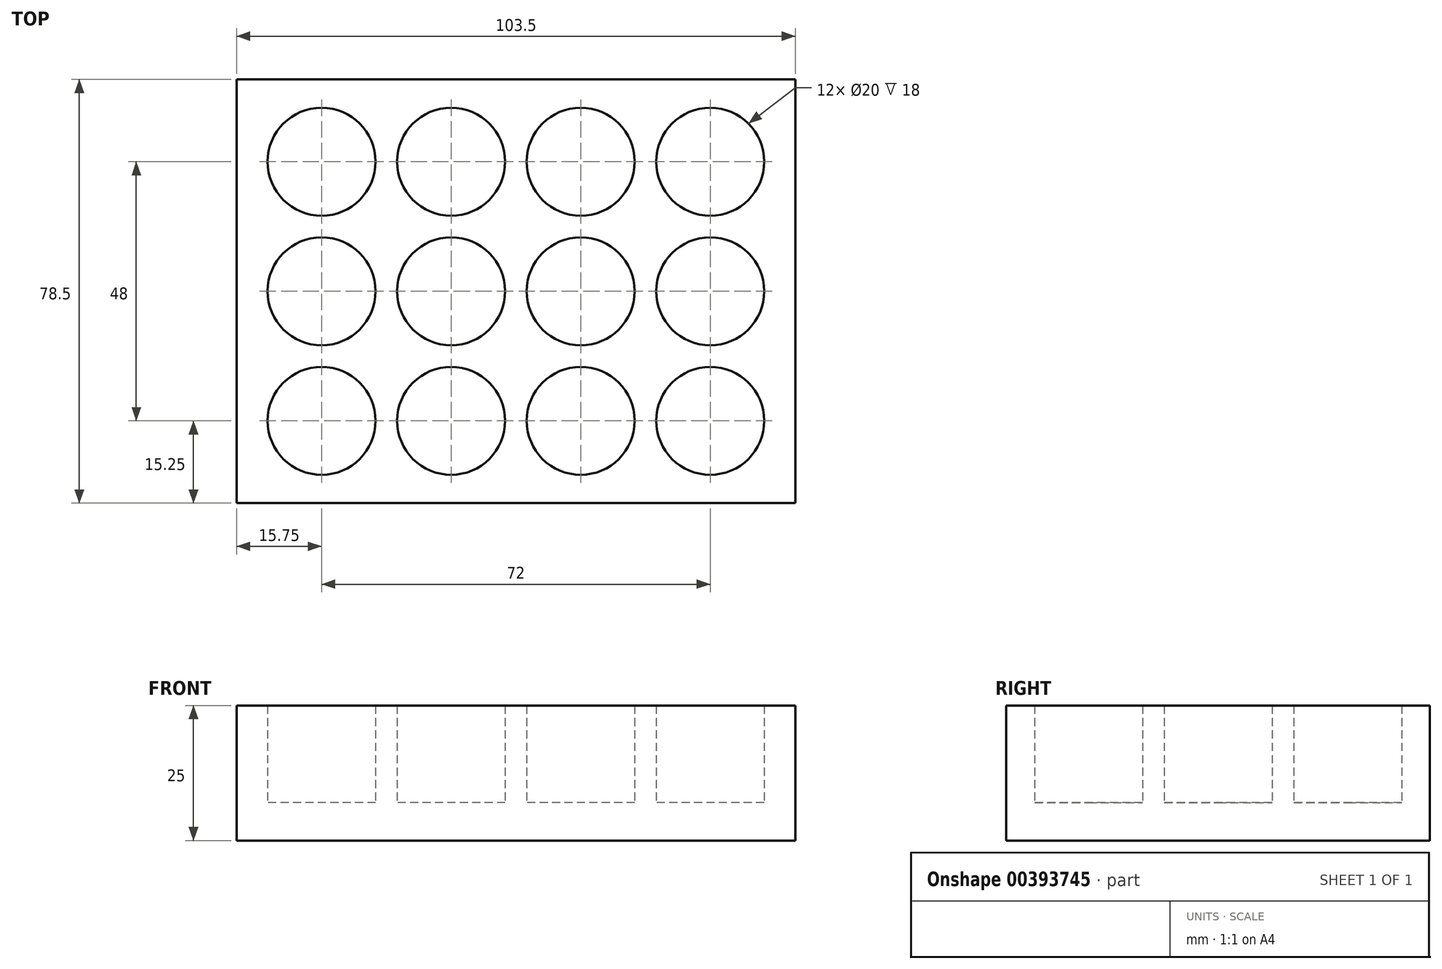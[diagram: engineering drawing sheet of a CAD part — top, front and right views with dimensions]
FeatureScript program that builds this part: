
annotation { "Feature Type Name" : "Feature", "Feature Type Description" : "" }
export const myFeature = defineFeature(function(context is Context, id is Id, definition is map)
    precondition{}
    {
        {
            var Q0;
            Q0=qCreatedBy(makeId("Top.planeOp"),FACE);
            var sketch = newSketch(context, id + "F0", { "sketchPlane" : qUnion([Q0])});
            skLineSegment(sketch, "E0.bottom", {"start": v(51.75, 39.25) * mm, "end": v(-51.75, 39.25) * mm});
            skLineSegment(sketch, "E0.top", {"start": v(51.75, -39.25) * mm, "end": v(-51.75, -39.25) * mm});
            skLineSegment(sketch, "E0.left", {"start": v(51.75, 39.25) * mm, "end": v(51.75, -39.25) * mm});
            skLineSegment(sketch, "E0.right", {"start": v(-51.75, 39.25) * mm, "end": v(-51.75, -39.25) * mm});
            skPoint(sketch, "E0.middle", {"position": v(0, 0) * mm});
            skCircle(sketch, "E1", {"center": v(-36, -24) * mm, "radius": 10 * mm});
            skCircle(sketch, "E2.0.1.0", {"center": v(-36, 0) * mm, "radius": 10 * mm});
            skCircle(sketch, "E2.0.2.0", {"center": v(-36, 24) * mm, "radius": 10 * mm});
            skCircle(sketch, "E2.1.0.0", {"center": v(-12, -24) * mm, "radius": 10 * mm});
            skCircle(sketch, "E2.1.1.0", {"center": v(-12, 0) * mm, "radius": 10 * mm});
            skCircle(sketch, "E2.1.2.0", {"center": v(-12, 24) * mm, "radius": 10 * mm});
            skCircle(sketch, "E2.2.0.0", {"center": v(12, -24) * mm, "radius": 10 * mm});
            skCircle(sketch, "E2.2.1.0", {"center": v(12, 0) * mm, "radius": 10 * mm});
            skCircle(sketch, "E2.2.2.0", {"center": v(12, 24) * mm, "radius": 10 * mm});
            skCircle(sketch, "E2.3.0.0", {"center": v(36, -24) * mm, "radius": 10 * mm});
            skCircle(sketch, "E2.3.1.0", {"center": v(36, 0) * mm, "radius": 10 * mm});
            skCircle(sketch, "E2.3.2.0", {"center": v(36, 24) * mm, "radius": 10 * mm});
            skLineSegment(sketch, "E2.direction1", {"start": v(-36, -24) * mm, "end": v(-12, -24) * mm, "construction": true});
            skLineSegment(sketch, "E2.direction2", {"start": v(-36, -24) * mm, "end": v(-36, 0) * mm, "construction": true});
            skLineSegment(sketch, "E3", {"start": v(12, 0) * mm, "end": v(-12, 0) * mm, "construction": true});
            skSolve(sketch);
        }
        {
            var Q0;
            Q0=makeQuery(id+"F0.imprint","IMPRINT",FACE,{"disambiguationData":[TD([[makeQuery(id+"F0.imprint","IMPRINT",EDGE,{"derivedFrom":sQuery(id+"F0.wireOp",EDGE,"E0.bottom")}),1.0]])]});
            extrude(context, id + "F1", {"entities" : qUnion([Q0]), "depth" : 18 * mm});
        }
        {
            var Q0;
            Q0 = qSketchRegion(id + "F0", true);
            var Q1;
            Q1=makeQuery(id+"F0.imprint","IMPRINT",FACE,{"disambiguationData":[TD([[makeQuery(id+"F0.imprint","IMPRINT",EDGE,{"derivedFrom":sQuery(id+"F0.wireOp",EDGE,"E1")}),1.0]])]});
            var Q2;
            Q2=makeQuery(id+"F0.imprint","IMPRINT",FACE,{"disambiguationData":[TD([[makeQuery(id+"F0.imprint","IMPRINT",EDGE,{"derivedFrom":sQuery(id+"F0.wireOp",EDGE,"E2.1.0.0")}),1.0]])]});
            var Q3;
            Q3=makeQuery(id+"F0.imprint","IMPRINT",FACE,{"disambiguationData":[TD([[makeQuery(id+"F0.imprint","IMPRINT",EDGE,{"derivedFrom":sQuery(id+"F0.wireOp",EDGE,"E2.2.0.0")}),1.0]])]});
            var Q4;
            Q4=makeQuery(id+"F0.imprint","IMPRINT",FACE,{"disambiguationData":[TD([[makeQuery(id+"F0.imprint","IMPRINT",EDGE,{"derivedFrom":sQuery(id+"F0.wireOp",EDGE,"E2.3.0.0")}),1.0]])]});
            var Q5;
            Q5=makeQuery(id+"F0.imprint","IMPRINT",FACE,{"disambiguationData":[TD([[makeQuery(id+"F0.imprint","IMPRINT",EDGE,{"derivedFrom":sQuery(id+"F0.wireOp",EDGE,"E2.2.1.0")}),1.0]])]});
            var Q6;
            Q6=makeQuery(id+"F0.imprint","IMPRINT",FACE,{"disambiguationData":[TD([[makeQuery(id+"F0.imprint","IMPRINT",EDGE,{"derivedFrom":sQuery(id+"F0.wireOp",EDGE,"E2.1.1.0")}),1.0]])]});
            var Q7;
            Q7=makeQuery(id+"F0.imprint","IMPRINT",FACE,{"disambiguationData":[TD([[makeQuery(id+"F0.imprint","IMPRINT",EDGE,{"derivedFrom":sQuery(id+"F0.wireOp",EDGE,"E2.0.1.0")}),1.0]])]});
            var Q8;
            Q8=makeQuery(id+"F0.imprint","IMPRINT",FACE,{"disambiguationData":[TD([[makeQuery(id+"F0.imprint","IMPRINT",EDGE,{"derivedFrom":sQuery(id+"F0.wireOp",EDGE,"E2.0.2.0")}),1.0]])]});
            var Q9;
            Q9=makeQuery(id+"F0.imprint","IMPRINT",FACE,{"disambiguationData":[TD([[makeQuery(id+"F0.imprint","IMPRINT",EDGE,{"derivedFrom":sQuery(id+"F0.wireOp",EDGE,"E2.1.2.0")}),1.0]])]});
            var Q10;
            Q10=makeQuery(id+"F0.imprint","IMPRINT",FACE,{"disambiguationData":[TD([[makeQuery(id+"F0.imprint","IMPRINT",EDGE,{"derivedFrom":sQuery(id+"F0.wireOp",EDGE,"E2.2.2.0")}),1.0]])]});
            var Q11;
            Q11=makeQuery(id+"F0.imprint","IMPRINT",FACE,{"disambiguationData":[TD([[makeQuery(id+"F0.imprint","IMPRINT",EDGE,{"derivedFrom":sQuery(id+"F0.wireOp",EDGE,"E2.3.2.0")}),1.0]])]});
            var Q12;
            Q12=makeQuery(id+"F0.imprint","IMPRINT",FACE,{"disambiguationData":[TD([[makeQuery(id+"F0.imprint","IMPRINT",EDGE,{"derivedFrom":sQuery(id+"F0.wireOp",EDGE,"E2.3.1.0")}),1.0]])]});
            extrude(context, id + "F2", {"entities" : qUnion([Q0, Q1, Q2, Q3, Q4, Q5, Q6, Q7, Q8, Q9, Q10, Q11, Q12]), "operationType" : NewBodyOperationType.ADD, "oppositeDirection" : true, "depth" : (25 - 18) * mm});
        }
    });
